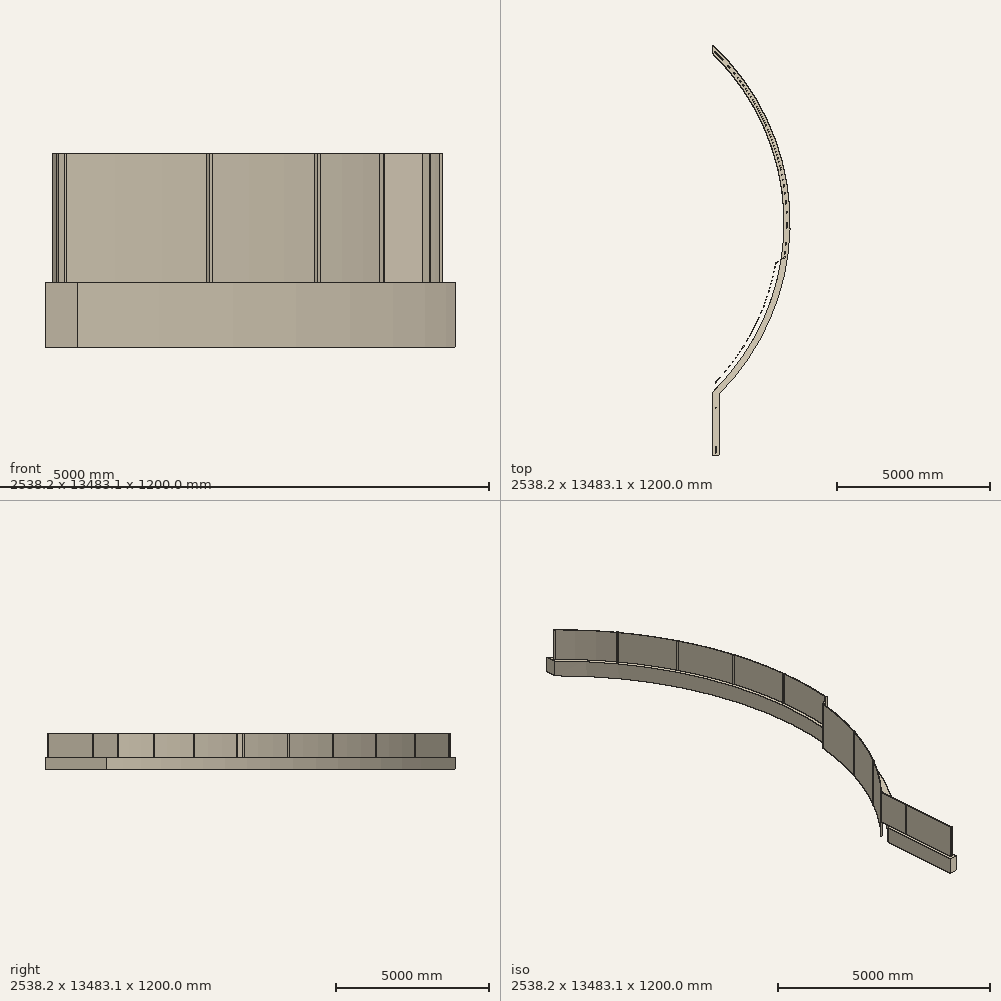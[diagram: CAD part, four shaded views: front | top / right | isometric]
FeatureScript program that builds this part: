
annotation { "Feature Type Name" : "Feature", "Feature Type Description" : "" }
export const myFeature = defineFeature(function(context is Context, id is Id, definition is map)
    precondition{}
    {
        {
            var Q0;
            Q0=qCreatedBy(makeId("Top.planeOp"),FACE);
            var sketch = newSketch(context, id + "F0", { "sketchPlane" : qUnion([Q0])});
            skLineSegment(sketch, "E0", {"start": v(0, -2000) * mm, "end": v(0, 0) * mm});
            skArc(sketch, "E1", {"start": v(0, 0) * mm, "mid": v(2337.01, 5784) * mm, "end": v(-200, 11483.1) * mm});
            skLineSegment(sketch, "E2", {"start": v(0, 0) * mm, "end": v(-200, -200) * mm, "construction": true});
            skArc(sketch, "E3", {"start": v(-200, 11206.48) * mm, "mid": v(2138.22, 5644.97) * mm, "end": v(-200, 83.46) * mm});
            skLineSegment(sketch, "E4", {"start": v(0, -2000) * mm, "end": v(-200, -2000) * mm});
            skLineSegment(sketch, "E5", {"start": v(-200, -2000) * mm, "end": v(-200, 83.46) * mm});
            skLineSegment(sketch, "E6", {"start": v(-200, 11483.1) * mm, "end": v(-200, 11206.48) * mm});
            skPoint(sketch, "E7", {"position": v(1968.13, 4026.7) * mm});
            skLineSegment(sketch, "E8", {"start": v(-200, 83.46) * mm, "end": v(-200, 11206.48) * mm, "construction": true});
            skLineSegment(sketch, "E9", {"start": v(-200, 11206.48) * mm, "end": v(1037.5, 9635.3) * mm, "construction": true});
            skSolve(sketch);
        }
        {
            var Q0;
            Q0 = qSketchRegion(id + "F0", true);
            extrude(context, id + "F1", {"entities" : qUnion([Q0]), "depth" : 400 * mm, "offsetDistance" : 25 * mm});
        }
        {
            var Q0;
            Q0=qCreatedBy(makeId("Top.planeOp"),FACE);
            var sketch = newSketch(context, id + "F2", { "sketchPlane" : qUnion([Q0])});
            skArc(sketch, "E10", {"start": v(1871.3, 4314.1) * mm, "mid": v(1172.46, 2211.56) * mm, "end": v(-100.78, 398.3) * mm});
            skLineSegment(sketch, "E11", {"start": v(1871.3, 4314.1) * mm, "end": v(1473.2, 2888.65) * mm, "construction": true});
            skLineSegment(sketch, "E12", {"start": v(1473.2, 2888.65) * mm, "end": v(807.5, 1566.82) * mm, "construction": true});
            skLineSegment(sketch, "E13", {"start": v(807.5, 1566.82) * mm, "end": v(-100.78, 398.3) * mm, "construction": true});
            skLineSegment(sketch, "E14.bottom", {"start": v(1894.49, 4330.3) * mm, "end": v(1855.1, 4337.28) * mm});
            skLineSegment(sketch, "E14.top", {"start": v(1887.51, 4290.92) * mm, "end": v(1848.13, 4297.9) * mm});
            skLineSegment(sketch, "E14.left", {"start": v(1894.49, 4330.3) * mm, "end": v(1887.51, 4290.92) * mm});
            skLineSegment(sketch, "E14.right", {"start": v(1855.1, 4337.28) * mm, "end": v(1848.13, 4297.9) * mm});
            skPoint(sketch, "E14.middle", {"position": v(1871.3, 4314.1) * mm});
            skLineSegment(sketch, "E15", {"start": v(1891, 4310.61) * mm, "end": v(1851.61, 4317.58) * mm, "construction": true});
            skLineSegment(sketch, "E16.bottom", {"start": v(1484.63, 2862.77) * mm, "end": v(1447.33, 2877.22) * mm});
            skLineSegment(sketch, "E16.top", {"start": v(1499.07, 2900.08) * mm, "end": v(1461.77, 2914.52) * mm});
            skLineSegment(sketch, "E16.left", {"start": v(1484.63, 2862.77) * mm, "end": v(1499.07, 2900.08) * mm});
            skLineSegment(sketch, "E16.right", {"start": v(1447.33, 2877.22) * mm, "end": v(1461.77, 2914.52) * mm});
            skPoint(sketch, "E16.middle", {"position": v(1473.2, 2888.65) * mm});
            skLineSegment(sketch, "E17", {"start": v(1454.55, 2895.87) * mm, "end": v(1491.85, 2881.42) * mm, "construction": true});
            skLineSegment(sketch, "E18.bottom", {"start": v(813.72, 1539.22) * mm, "end": v(779.9, 1560.6) * mm});
            skLineSegment(sketch, "E18.top", {"start": v(835.09, 1573.04) * mm, "end": v(801.27, 1594.4) * mm});
            skLineSegment(sketch, "E18.left", {"start": v(813.72, 1539.22) * mm, "end": v(835.09, 1573.04) * mm});
            skLineSegment(sketch, "E18.right", {"start": v(779.9, 1560.6) * mm, "end": v(801.27, 1594.4) * mm});
            skPoint(sketch, "E18.middle", {"position": v(807.5, 1566.82) * mm});
            skLineSegment(sketch, "E19", {"start": v(824.4, 1556.13) * mm, "end": v(790.59, 1577.5) * mm, "construction": true});
            skPoint(sketch, "E20.middle", {"position": v(-100.78, 398.3) * mm});
            skLineSegment(sketch, "E21.bottom", {"start": v(-101.56, 426.57) * mm, "end": v(-72.5, 399.08) * mm});
            skLineSegment(sketch, "E21.top", {"start": v(-129.05, 397.52) * mm, "end": v(-100, 370.02) * mm});
            skLineSegment(sketch, "E21.left", {"start": v(-101.56, 426.57) * mm, "end": v(-129.05, 397.52) * mm});
            skLineSegment(sketch, "E21.right", {"start": v(-72.5, 399.08) * mm, "end": v(-100, 370.02) * mm});
            skLineSegment(sketch, "E22", {"start": v(-86.25, 384.55) * mm, "end": v(-115.3, 412.04) * mm, "construction": true});
            skArc(sketch, "E23.0", {"start": v(1857.95, 4296.15) * mm, "mid": v(1158.38, 2205.86) * mm, "end": v(-110, 403.1) * mm});
            skLineSegment(sketch, "E24", {"start": v(-100.78, 398.3) * mm, "end": v(-100, -2000) * mm, "construction": true});
            skSolve(sketch);
        }
        {
            var Q0;
            Q0 = qSketchRegion(id + "F2", true);
            extrude(context, id + "F3", {"entities" : qUnion([Q0]), "operationType" : NewBodyOperationType.ADD, "depth" : 1200 * mm, "offsetDistance" : 25 * mm});
        }
        {
            var Q0;
            Q0=makeQuery(id+"F1.opExtrude","CAP_FACE",FACE,{"disambiguationData":[OSD([sQuery(id+"F0.wireOp",EDGE,"E0"),sQuery(id+"F0.wireOp",EDGE,"E1"),sQuery(id+"F0.wireOp",EDGE,"E3"),sQuery(id+"F0.wireOp",EDGE,"E4"),sQuery(id+"F0.wireOp",EDGE,"E5"),sQuery(id+"F0.wireOp",EDGE,"E6")])],"isStart":false});
            var sketch = newSketch(context, id + "F4", { "sketchPlane" : qUnion([Q0])});
            skLineSegment(sketch, "E25", {"start": v(-200, 11206.48) * mm, "end": v(-60.08, 11349.4) * mm, "construction": true});
            skLineSegment(sketch, "E26", {"start": v(-129.33, 11277.24) * mm, "end": v(826.2, 10147.04) * mm, "construction": true});
            skLineSegment(sketch, "E27.bottom", {"start": v(-129.03, 11248.96) * mm, "end": v(-157.61, 11276.94) * mm});
            skLineSegment(sketch, "E27.top", {"start": v(-101.04, 11277.54) * mm, "end": v(-129.62, 11305.52) * mm});
            skLineSegment(sketch, "E27.left", {"start": v(-129.62, 11305.52) * mm, "end": v(-157.61, 11276.94) * mm});
            skLineSegment(sketch, "E27.right", {"start": v(-101.04, 11277.54) * mm, "end": v(-129.03, 11248.96) * mm});
            skPoint(sketch, "E27.middle", {"position": v(-129.33, 11277.24) * mm});
            skLineSegment(sketch, "E28", {"start": v(-115.33, 11291.53) * mm, "end": v(-143.32, 11262.95) * mm, "construction": true});
            skLineSegment(sketch, "E29.bottom", {"start": v(821.21, 10119.2) * mm, "end": v(798.37, 10152.04) * mm});
            skLineSegment(sketch, "E29.top", {"start": v(854.05, 10142.04) * mm, "end": v(831.2, 10174.88) * mm});
            skLineSegment(sketch, "E29.left", {"start": v(821.21, 10119.2) * mm, "end": v(854.05, 10142.04) * mm});
            skLineSegment(sketch, "E29.right", {"start": v(798.37, 10152.04) * mm, "end": v(831.2, 10174.88) * mm});
            skPoint(sketch, "E29.middle", {"position": v(826.2, 10147.04) * mm});
            skLineSegment(sketch, "E30", {"start": v(809.79, 10135.62) * mm, "end": v(842.63, 10158.46) * mm, "construction": true});
            skLineSegment(sketch, "E31", {"start": v(826.2, 10147.04) * mm, "end": v(1553.65, 8858.16) * mm, "construction": true});
            skLineSegment(sketch, "E32.bottom", {"start": v(1563.77, 8884.57) * mm, "end": v(1527.24, 8868.27) * mm});
            skLineSegment(sketch, "E32.top", {"start": v(1580.07, 8848.05) * mm, "end": v(1543.54, 8831.74) * mm});
            skLineSegment(sketch, "E32.left", {"start": v(1563.77, 8884.57) * mm, "end": v(1580.07, 8848.05) * mm});
            skLineSegment(sketch, "E32.right", {"start": v(1527.24, 8868.27) * mm, "end": v(1543.54, 8831.74) * mm});
            skPoint(sketch, "E32.middle", {"position": v(1553.65, 8858.16) * mm});
            skLineSegment(sketch, "E33", {"start": v(1571.92, 8866.3) * mm, "end": v(1535.4, 8850) * mm, "construction": true});
            skLineSegment(sketch, "E34", {"start": v(1553.65, 8858.16) * mm, "end": v(2027.37, 7456.02) * mm, "construction": true});
            skLineSegment(sketch, "E35.bottom", {"start": v(2051.43, 7441.15) * mm, "end": v(2042.24, 7480.08) * mm});
            skLineSegment(sketch, "E35.top", {"start": v(2012.5, 7431.96) * mm, "end": v(2003.31, 7470.89) * mm});
            skLineSegment(sketch, "E35.left", {"start": v(2051.43, 7441.15) * mm, "end": v(2012.5, 7431.96) * mm});
            skLineSegment(sketch, "E35.right", {"start": v(2042.24, 7480.08) * mm, "end": v(2003.31, 7470.89) * mm});
            skPoint(sketch, "E35.middle", {"position": v(2027.37, 7456.02) * mm});
            skLineSegment(sketch, "E36", {"start": v(2046.84, 7460.61) * mm, "end": v(2007.9, 7451.42) * mm, "construction": true});
            skLineSegment(sketch, "E37", {"start": v(2027.37, 7456.02) * mm, "end": v(2230.67, 5990.05) * mm, "construction": true});
            skArc(sketch, "E38", {"start": v(-129.33, 11277.24) * mm, "mid": v(1823.5, 8168.23) * mm, "end": v(2156.37, 4511.91) * mm});
            skLineSegment(sketch, "E39", {"start": v(2230.67, 5990.05) * mm, "end": v(2156.37, 4511.91) * mm, "construction": true});
            skLineSegment(sketch, "E40.bottom", {"start": v(2249.77, 6010.9) * mm, "end": v(2209.81, 6009.15) * mm});
            skLineSegment(sketch, "E40.top", {"start": v(2251.52, 5970.94) * mm, "end": v(2211.56, 5969.2) * mm});
            skLineSegment(sketch, "E40.left", {"start": v(2249.77, 6010.9) * mm, "end": v(2251.52, 5970.94) * mm});
            skLineSegment(sketch, "E40.right", {"start": v(2209.81, 6009.15) * mm, "end": v(2211.56, 5969.2) * mm});
            skPoint(sketch, "E40.middle", {"position": v(2230.67, 5990.05) * mm});
            skLineSegment(sketch, "E41", {"start": v(2210.69, 5989.17) * mm, "end": v(2250.65, 5990.92) * mm, "construction": true});
            skLineSegment(sketch, "E42.bottom", {"start": v(2179.04, 4528.83) * mm, "end": v(2139.45, 4534.58) * mm});
            skLineSegment(sketch, "E42.top", {"start": v(2173.29, 4489.25) * mm, "end": v(2133.7, 4495) * mm});
            skLineSegment(sketch, "E42.left", {"start": v(2179.04, 4528.83) * mm, "end": v(2173.29, 4489.25) * mm});
            skLineSegment(sketch, "E42.right", {"start": v(2139.45, 4534.58) * mm, "end": v(2133.7, 4495) * mm});
            skPoint(sketch, "E42.middle", {"position": v(2156.37, 4511.91) * mm});
            skLineSegment(sketch, "E43", {"start": v(2136.58, 4514.79) * mm, "end": v(2176.16, 4509.04) * mm, "construction": true});
            skArc(sketch, "E44.0", {"start": v(-137.04, 11270.8) * mm, "mid": v(1813.7, 8165.97) * mm, "end": v(2146.62, 4514.34) * mm});
            skArc(sketch, "E45", {"start": v(-129.33, 11277.24) * mm, "mid": v(-129.68, 11277.6) * mm, "end": v(-130.04, 11277.94) * mm, "construction": true});
            skLineSegment(sketch, "E46", {"start": v(2156.37, 4511.91) * mm, "end": v(1871.3, 4314.1) * mm});
            skLineSegment(sketch, "E47.0", {"start": v(2150.01, 4519.67) * mm, "end": v(1865.63, 4322.33) * mm});
            skLineSegment(sketch, "E48", {"start": v(1871.3, 4314.1) * mm, "end": v(1865.63, 4322.33) * mm});
            skSolve(sketch);
        }
        {
            var Q0;
            Q0 = qSketchRegion(id + "F4", true);
            extrude(context, id + "F5", {"entities" : qUnion([Q0]), "operationType" : NewBodyOperationType.ADD, "depth" : 800 * mm, "offsetDistance" : 25 * mm});
        }
        {
            var Q0;
            Q0=makeQuery(id+"F1.opExtrude","CAP_FACE",FACE,{"disambiguationData":[OSD([sQuery(id+"F0.wireOp",EDGE,"E0"),sQuery(id+"F0.wireOp",EDGE,"E1"),sQuery(id+"F0.wireOp",EDGE,"E3"),sQuery(id+"F0.wireOp",EDGE,"E4"),sQuery(id+"F0.wireOp",EDGE,"E5"),sQuery(id+"F0.wireOp",EDGE,"E6")])],"isStart":false});
            var sketch = newSketch(context, id + "F6", { "sketchPlane" : qUnion([Q0])});
            skLineSegment(sketch, "E49.bottom", {"start": v(-80.02, -1910) * mm, "end": v(-120.02, -1910) * mm});
            skLineSegment(sketch, "E49.top", {"start": v(-80.02, -1950) * mm, "end": v(-120.02, -1950) * mm});
            skLineSegment(sketch, "E49.left", {"start": v(-80.02, -1910) * mm, "end": v(-80.02, -1950) * mm});
            skLineSegment(sketch, "E49.right", {"start": v(-120.02, -1910) * mm, "end": v(-120.02, -1950) * mm});
            skPoint(sketch, "E49.middle", {"position": v(-100.02, -1930) * mm});
            skLineSegment(sketch, "E50.bottom", {"start": v(-80.51, -410) * mm, "end": v(-120.51, -410) * mm});
            skLineSegment(sketch, "E50.top", {"start": v(-80.51, -450) * mm, "end": v(-120.51, -450) * mm});
            skLineSegment(sketch, "E50.left", {"start": v(-80.51, -410) * mm, "end": v(-80.51, -450) * mm});
            skLineSegment(sketch, "E50.right", {"start": v(-120.51, -410) * mm, "end": v(-120.51, -450) * mm});
            skPoint(sketch, "E50.middle", {"position": v(-100.51, -430) * mm});
            skLineSegment(sketch, "E51", {"start": v(-100.78, 398.3) * mm, "end": v(-100.02, -1930) * mm});
            skLineSegment(sketch, "E52.0", {"start": v(-110.78, 398.3) * mm, "end": v(-110.02, -1930) * mm});
            skLineSegment(sketch, "E53", {"start": v(-110.78, 398.3) * mm, "end": v(-100.78, 398.3) * mm});
            skSolve(sketch);
        }
        {
            var Q0;
            Q0 = qSketchRegion(id + "F6", true);
            extrude(context, id + "F7", {"entities" : qUnion([Q0]), "operationType" : NewBodyOperationType.ADD, "depth" : 800 * mm, "offsetDistance" : 25 * mm});
        }
    });
